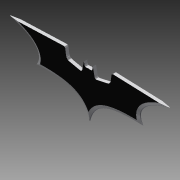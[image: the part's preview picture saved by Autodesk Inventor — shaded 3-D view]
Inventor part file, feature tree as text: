
AUTODESK INVENTOR PART (.ipt)
format: ipt  version: 2014 (Build 180170000, 170)  size: 288,768 bytes
history: native  units: in
note: dims shown in document units (in); Inventor stores cm internally (conversion verified against a paired STEP export)
features: chamfer x2, extrude x1, sketch x1
ambient origin geometry x8: Origin, YZ Plane, XZ Plane, XY Plane, X Axis, Y Axis, Z Axis, Center Point
bodies: Solid1 (feature_tree)
feature tree (4):
  extrude  "Extrusion1"  Depth=0.3in
  chamfer  "Chamfer1"  Distance=0.125in
  chamfer  "Chamfer2"  Distance=0.125in
  sketch  "Sketch1"  dims[d1=0.125in d2=0.3in d4=0.125in d5=0.125in d19=0.25in d20=0.0in d21=0.12in d22=0.125in d23=45.0deg d24=0.12in d25=0.125in d26=45.0deg]
